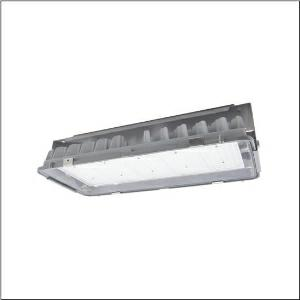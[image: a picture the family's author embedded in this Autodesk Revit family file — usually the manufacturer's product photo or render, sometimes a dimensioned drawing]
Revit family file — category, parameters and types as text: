
# Revit family: highbay_11xtreme_51hf61da4hma
name_source: partatom
category: Lighting Fixtures
units: mm (PartAtom-declared; Revit-internal decimal feet)

## family parameters
Cut with Voids When Loaded = No
Host = Face
Light Source = No
Part Type = Normal
Room Calculation Point = No
Round Connector Dimension = Use Diameter
Shared = No

## types (1)
- --- (1 x LED, 18700 lm, 96.3 W, 4000K)
    Apparent Load = 96 VA
    CIE Flux Codes = 88 96 99 100 100
    Color Rendering = 80
    Color Temperature = 4000K
    Default Elevation = 1800 mm
    Description = Highbay 11Xtreme, high bay luminaire, primary light control with lens, of PMMA, primary optical cover: cover, of toughened safety glass, light emission: direct distribution, primary light characteristic: symmetric, installation type: suspended mounting, surface-mounted, 1x LED module,for 1x LED, rated luminous flux: 18.700lm, luminous efficacy: 194lm/W, light colour: 840, colour temperature: 4000K, control gear: DALI 2, with cable H07RN-F 5x 1.5mm², mains connection: 220..240V, AC, 50/60Hz, cable length: 1,5m, rated input power: 96W, luminaire housing, of diecast aluminium, coated, silver, length: 595mm, width: 280mm, height: 195mm, protection rating (complete): IP66, insulation class (complete): insulation class I (protective earthing), certification: CE, ENEC, UKCA, protection symbol: D, ball protection: ball impact resistant according to DIN VDE 0710 part 13 (with chain suspension), impact resistance: IK08, permissible operating ambient temperature: -25..+70°C, reducing of maximum allowable ambient temperature of 5°C with ceiling mounting, packaging unit: 1 piece
    Height = 157 mm
    Lamp = 1 x LED
    Lamp Light Flux = 18700 lm
    Lamp Power = 96.3 W
    Lamp count = 1
    Length = 593 mm
    Luminous efficacy = 194 lm/W
    Manufacturer = Siteco
    ModVariant = No
    Model = 51HF61DA4HMA
    Mounting Place = Ceiling
    Mounting Type = Pendant
    Number of Poles = 1
    OnlyDefault = Yes
    Power Factor = 1
    Product Name = Highbay 11Xtreme
    Product group = high bay luminaire
    ProductGroupID = 902
    Protection Class = Protection class I
    Protection Degree = IP 66
    RLX_Detail_Level = 1
    RLX_Emergency_Light_Flux = 0 lm
    RLX_Emergency_Type = 0
    RLX_Emergency_Type_DB = No
    RlxData = <blob elided: 27749 chars, md5=28dc6d4e>
    Socket = socket
    Standby Power = 0 W
    System Light Flux = 18700 lm
    System Power = 96 W
    Type Comments = factory setting: luminous flux: 100 % | dim-lin: 254 | 650 mA
    Type Image = l_1258342.jpg
    URL = http://relux.com
    VarID = @adj_088617
    Voltage = 0 V
    Weight = 0.00 kg
    Width = 278 mm

## geometry (parser evidence)
native form markers: Blend x4, Sweep x14
no freeform markers — native parametric forms only
